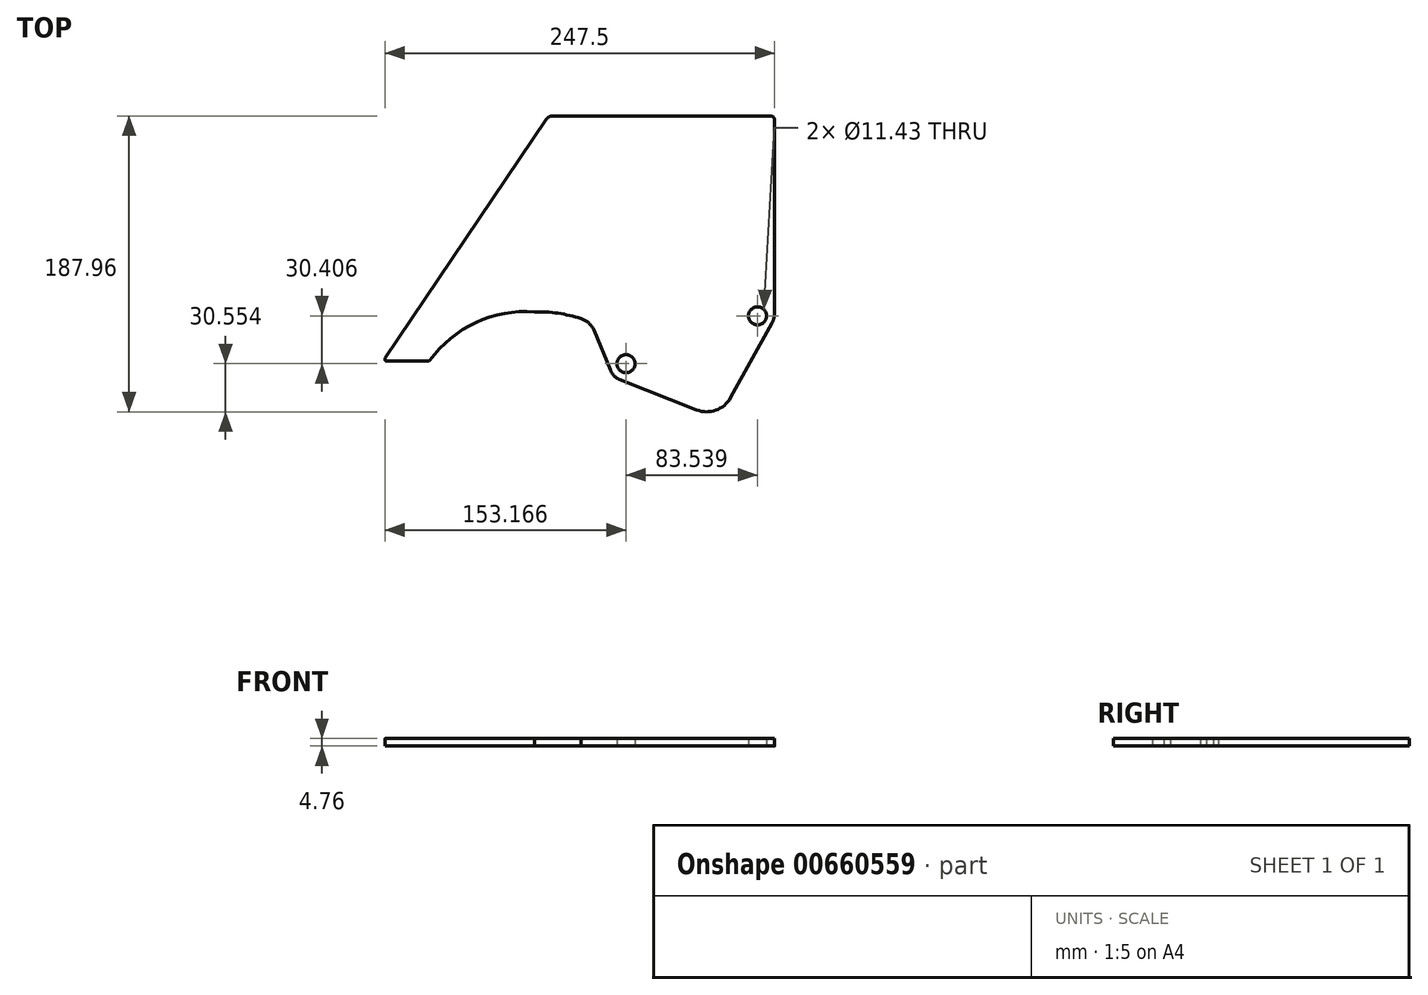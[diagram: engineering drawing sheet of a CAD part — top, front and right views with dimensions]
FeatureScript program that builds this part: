
annotation { "Feature Type Name" : "Feature", "Feature Type Description" : "" }
export const myFeature = defineFeature(function(context is Context, id is Id, definition is map)
    precondition{}
    {
        {
            var Q0;
            Q0=qCreatedBy(makeId("Top.planeOp"),FACE);
            var sketch = newSketch(context, id + "F0", { "sketchPlane" : qUnion([Q0])});
            skLineSegment(sketch, "E0.bottom", {"start": v(0, 0) * mm, "end": v(-143.51, 0) * mm});
            skLineSegment(sketch, "E0.top", {"start": v(-2.54, 187.96) * mm, "end": v(-140.8, 187.96) * mm});
            skLineSegment(sketch, "E0.left", {"start": v(0, 62.6) * mm, "end": v(0, 185.42) * mm});
            skLineSegment(sketch, "E0.right", {"start": v(-143.51, 0) * mm, "end": v(-143.51, 187.96) * mm});
            skLineSegment(sketch, "E1", {"start": v(-145.02, 185.72) * mm, "end": v(-247.28, 34.11) * mm});
            skLineSegment(sketch, "E2", {"start": v(-246.23, 32.13) * mm, "end": v(-220.05, 32.13) * mm});
            skCircle(sketch, "E3", {"center": v(-10.8, 60.96) * mm, "radius": 5.72 * mm});
            skCircle(sketch, "E4", {"center": v(-94.33, 30.55) * mm, "radius": 5.72 * mm});
            skLineSegment(sketch, "E5", {"start": v(-1.6, 56.45) * mm, "end": v(-27.9, 9) * mm});
            skCircle(sketch, "E6", {"center": v(-43.17, 17.46) * mm, "radius": 17.46 * mm});
            skLineSegment(sketch, "E7", {"start": v(-10.8, 60.96) * mm, "end": v(-94.33, 30.55) * mm});
            skCircle(sketch, "E8.0", {"center": v(-94.33, 30.55) * mm, "radius": 10.8 * mm});
            skLineSegment(sketch, "E9", {"start": v(-98.3, 20.52) * mm, "end": v(-49.14, 1.05) * mm});
            skLineSegment(sketch, "E10", {"start": v(-104.31, 26.44) * mm, "end": v(-114.78, 51.84) * mm});
            skPoint(sketch, "E11", {"position": v(-152.4, 63.5) * mm});
            skPoint(sketch, "E12", {"position": v(-127, 59.69) * mm});
            skCircle(sketch, "E13", {"center": v(-126.52, 47) * mm, "radius": 12.7 * mm});
            skPoint(sketch, "E14.newPointA", {"position": v(0, 0) * mm});
            skPoint(sketch, "E14.newPointB", {"position": v(0.91, 60.96) * mm});
            skArc(sketch, "E14.filletArc", {"start": v(-1.6, 56.45) * mm, "mid": v(-0.4, 59.42) * mm, "end": v(0, 62.6) * mm});
            skPoint(sketch, "E15.visualSharp", {"position": v(-248.62, 32.13) * mm});
            skArc(sketch, "E15.filletArc", {"start": v(-247.28, 34.11) * mm, "mid": v(-247.35, 32.8) * mm, "end": v(-246.23, 32.13) * mm});
            skPoint(sketch, "E16.visualSharp", {"position": v(-219.4, 32.13) * mm});
            skPoint(sketch, "E17.visualSharp", {"position": v(-143.51, 187.96) * mm});
            skArc(sketch, "E17.filletArc", {"start": v(-140.8, 187.96) * mm, "mid": v(-143.2, 187.37) * mm, "end": v(-145.02, 185.72) * mm});
            skPoint(sketch, "E18.visualSharp", {"position": v(0, 187.96) * mm});
            skArc(sketch, "E18.filletArc", {"start": v(0, 185.42) * mm, "mid": v(-0.74, 187.22) * mm, "end": v(-2.54, 187.96) * mm});
            skPoint(sketch, "E19.orphan", {"position": v(-116.45, 55.88) * mm});
            skArc(sketch, "E20", {"start": v(-152.4, 63.5) * mm, "mid": v(-189.69, 56.66) * mm, "end": v(-219.03, 32.65) * mm});
            skArc(sketch, "E21.filletArc", {"start": v(-220.05, 32.13) * mm, "mid": v(-219.48, 32.27) * mm, "end": v(-219.03, 32.65) * mm});
            skArc(sketch, "E22", {"start": v(-122.96, 59.19) * mm, "mid": v(-137.5, 62.6) * mm, "end": v(-152.4, 63.5) * mm});
            skSolve(sketch);
        }
        {
            var Q0;
            {var subQ4=sQuery(id+"F0.wireOp",EDGE,"E1");Q0=makeQuery(id+"F0.imprint","IMPRINT",FACE,{"disambiguationData":[TD([[makeQuery(id+"F0.imprint","IMPRINT",EDGE,{"derivedFrom":subQ4}),1.0]])]});}
            var Q1;
            {var subQ7=sQuery(id+"F0.wireOp",EDGE,"E0.top");Q1=makeQuery(id+"F0.imprint","IMPRINT",FACE,{"disambiguationData":[TD([[makeQuery(id+"F0.imprint","IMPRINT",EDGE,{"derivedFrom":subQ7}),1.0]])]});}
            var Q2;
            {var subQ0=sQuery(id+"F0.wireOp",EDGE,"E6");var subQ1=makeQuery(id+"F0.imprint","INTERSECT",VERTEX,{"derivedFrom":[sQuery(id+"F0.wireOp",EDGE,"E0.bottom"),subQ0]});Q2=makeQuery(id+"F0.imprint","IMPRINT",FACE,{"disambiguationData":[TD([[makeQuery(id+"F0.imprint","IMPRINT",EDGE,{"disambiguationData":[TD([[subQ1,1.0]])],"derivedFrom":subQ0}),1.0]])]});}
            var Q3;
            Q3=makeQuery(id+"F0.imprint","IMPRINT",FACE,{"disambiguationData":[TD([[makeQuery(id+"F0.imprint","IMPRINT",EDGE,{"derivedFrom":sQuery(id+"F0.wireOp",EDGE,"E4")}),-1.0]])]});
            extrude(context, id + "F1", {"entities" : qUnion([Q0, Q1, Q2, Q3]), "depth" : 4.76 * mm, "offsetDistance" : 25.4 * mm});
        }
    });
